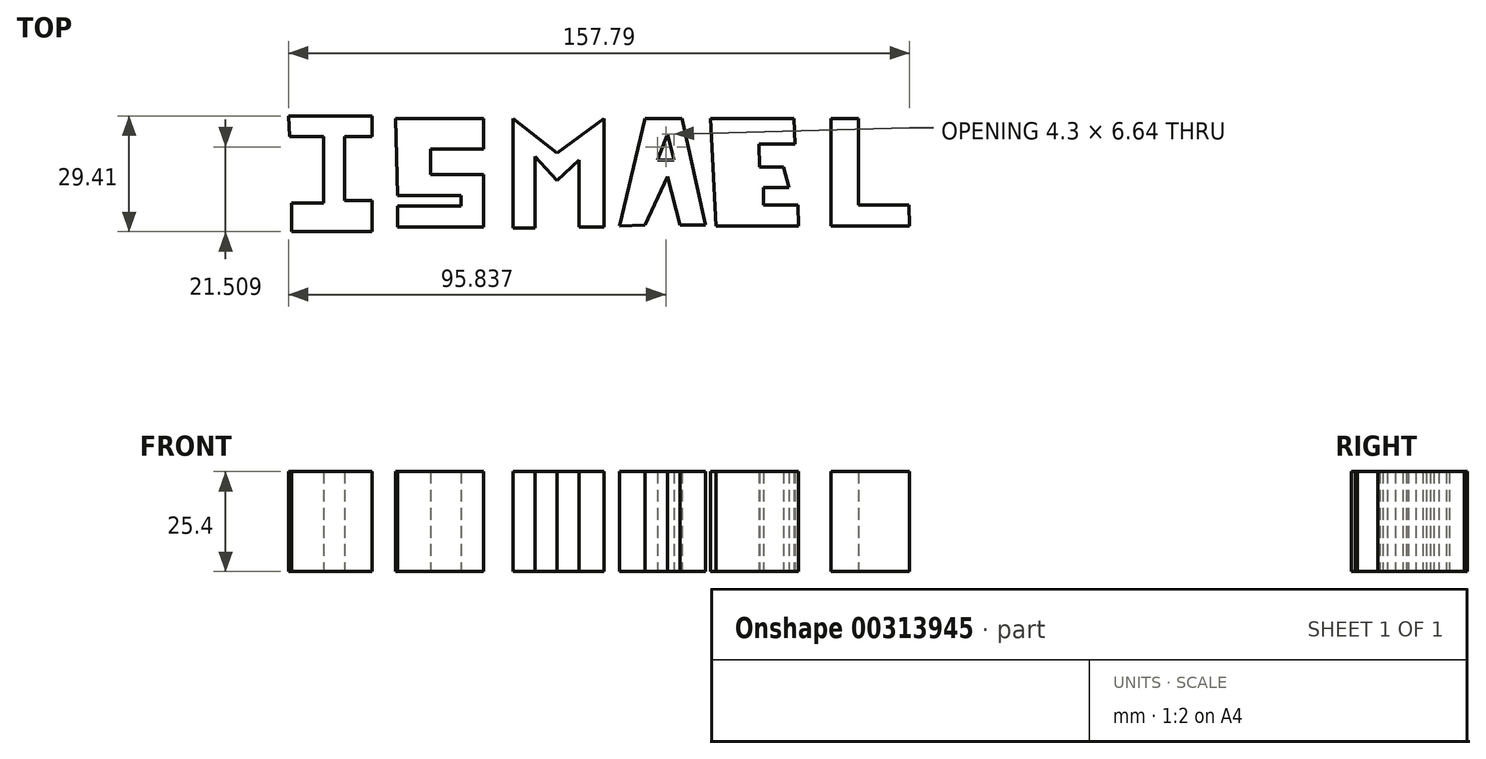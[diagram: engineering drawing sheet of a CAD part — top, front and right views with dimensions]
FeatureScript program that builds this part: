
annotation { "Feature Type Name" : "Feature", "Feature Type Description" : "" }
export const myFeature = defineFeature(function(context is Context, id is Id, definition is map)
    precondition{}
    {
        {
            var Q0;
            Q0=qCreatedBy(makeId("Top.planeOp"),FACE);
            var sketch = newSketch(context, id + "F0", { "sketchPlane" : qUnion([Q0])});
            skLineSegment(sketch, "E0", {"start": v(-96.24, 33.02) * mm, "end": v(-75.04, 33.02) * mm});
            skLineSegment(sketch, "E1", {"start": v(-75.04, 33.02) * mm, "end": v(-75.04, 27.71) * mm});
            skLineSegment(sketch, "E2", {"start": v(-75.04, 27.71) * mm, "end": v(-82.03, 27.71) * mm});
            skLineSegment(sketch, "E3", {"start": v(-82.03, 27.71) * mm, "end": v(-82.03, 11.57) * mm});
            skLineSegment(sketch, "E4", {"start": v(-82.03, 11.57) * mm, "end": v(-75.04, 11.57) * mm});
            skLineSegment(sketch, "E5", {"start": v(-75.04, 11.57) * mm, "end": v(-75.04, 3.61) * mm});
            skLineSegment(sketch, "E6", {"start": v(-75.04, 3.61) * mm, "end": v(-95.52, 3.61) * mm});
            skLineSegment(sketch, "E7", {"start": v(-95.52, 3.61) * mm, "end": v(-95.52, 10.84) * mm});
            skLineSegment(sketch, "E8", {"start": v(-95.52, 10.84) * mm, "end": v(-87.33, 10.84) * mm});
            skLineSegment(sketch, "E9", {"start": v(-87.33, 10.84) * mm, "end": v(-87.33, 27.71) * mm});
            skLineSegment(sketch, "E10", {"start": v(-87.33, 27.71) * mm, "end": v(-96, 27.71) * mm});
            skLineSegment(sketch, "E11", {"start": v(-96, 27.71) * mm, "end": v(-96.24, 33.02) * mm});
            skSolve(sketch);
        }
        {
            var Q0;
            Q0=makeQuery(id+"F0.imprint","IMPRINT",FACE,{"disambiguationData":[TD([[makeQuery(id+"F0.imprint","IMPRINT",EDGE,{"derivedFrom":sQuery(id+"F0.wireOp",EDGE,"E0")}),-1.0]])]});
            extrude(context, id + "F1", {"entities" : qUnion([Q0]), "depth" : 25.4 * mm});
        }
        {
            var Q0;
            Q0=qCreatedBy(makeId("Top.planeOp"),FACE);
            var sketch = newSketch(context, id + "F2", { "sketchPlane" : qUnion([Q0])});
            skLineSegment(sketch, "E12", {"start": v(-69.07, 32.3) * mm, "end": v(-46.65, 32.3) * mm});
            skLineSegment(sketch, "E13", {"start": v(-46.65, 32.3) * mm, "end": v(-46.65, 24.58) * mm});
            skLineSegment(sketch, "E14", {"start": v(-46.65, 24.58) * mm, "end": v(-60.15, 24.58) * mm});
            skLineSegment(sketch, "E15", {"start": v(-60.15, 24.58) * mm, "end": v(-60.15, 18.07) * mm});
            skLineSegment(sketch, "E16", {"start": v(-60.15, 18.07) * mm, "end": v(-46.65, 18.07) * mm});
            skLineSegment(sketch, "E17", {"start": v(-46.65, 18.07) * mm, "end": v(-46.65, 4.82) * mm});
            skLineSegment(sketch, "E18", {"start": v(-46.65, 4.82) * mm, "end": v(-68.58, 4.82) * mm});
            skLineSegment(sketch, "E19", {"start": v(-68.58, 4.82) * mm, "end": v(-68.58, 10.12) * mm});
            skLineSegment(sketch, "E20", {"start": v(-68.58, 10.12) * mm, "end": v(-52.44, 10.12) * mm});
            skLineSegment(sketch, "E21", {"start": v(-52.44, 10.12) * mm, "end": v(-52.44, 12.77) * mm});
            skLineSegment(sketch, "E22", {"start": v(-52.44, 12.77) * mm, "end": v(-68.58, 12.77) * mm});
            skLineSegment(sketch, "E23", {"start": v(-68.58, 12.77) * mm, "end": v(-69.07, 32.3) * mm});
            skLineSegment(sketch, "E24", {"start": v(-39.18, 32.3) * mm, "end": v(-39.18, 4.58) * mm});
            skLineSegment(sketch, "E25", {"start": v(-39.18, 4.58) * mm, "end": v(-33.64, 4.58) * mm});
            skLineSegment(sketch, "E26", {"start": v(-33.64, 4.58) * mm, "end": v(-33.64, 22.65) * mm});
            skLineSegment(sketch, "E27", {"start": v(-33.64, 22.65) * mm, "end": v(-28.1, 16.63) * mm});
            skLineSegment(sketch, "E28", {"start": v(-28.1, 16.63) * mm, "end": v(-22.47, 21.8) * mm});
            skLineSegment(sketch, "E29", {"start": v(-22.47, 21.8) * mm, "end": v(-22.47, 4.82) * mm});
            skLineSegment(sketch, "E30", {"start": v(-22.47, 4.82) * mm, "end": v(-16.05, 4.82) * mm});
            skLineSegment(sketch, "E31", {"start": v(-16.05, 4.82) * mm, "end": v(-16.05, 32.3) * mm});
            skLineSegment(sketch, "E32", {"start": v(-16.05, 32.3) * mm, "end": v(-28.1, 23.62) * mm});
            skLineSegment(sketch, "E33", {"start": v(-28.1, 23.62) * mm, "end": v(-39.18, 32.3) * mm});
            skLineSegment(sketch, "E34", {"start": v(-12.2, 5.06) * mm, "end": v(-5.68, 32.3) * mm});
            skLineSegment(sketch, "E35", {"start": v(-5.68, 32.3) * mm, "end": v(3.71, 32.3) * mm});
            skLineSegment(sketch, "E36", {"start": v(3.71, 32.3) * mm, "end": v(9.74, 5.3) * mm});
            skLineSegment(sketch, "E37", {"start": v(9.74, 5.3) * mm, "end": v(3.23, 5.3) * mm});
            skLineSegment(sketch, "E38", {"start": v(3.23, 5.3) * mm, "end": v(0, 17.6) * mm});
            skLineSegment(sketch, "E39", {"start": v(0, 17.6) * mm, "end": v(-5.68, 5.3) * mm});
            skLineSegment(sketch, "E40", {"start": v(-5.68, 5.3) * mm, "end": v(-12.2, 5.06) * mm});
            skLineSegment(sketch, "E41", {"start": v(-2.55, 21.8) * mm, "end": v(0, 28.44) * mm});
            skLineSegment(sketch, "E42", {"start": v(0, 28.44) * mm, "end": v(1.75, 21.8) * mm});
            skLineSegment(sketch, "E43", {"start": v(1.75, 21.8) * mm, "end": v(-2.55, 21.8) * mm});
            skLineSegment(sketch, "E44", {"start": v(10.94, 32.3) * mm, "end": v(32.15, 32.3) * mm});
            skLineSegment(sketch, "E45", {"start": v(32.15, 32.3) * mm, "end": v(32.4, 25.81) * mm});
            skLineSegment(sketch, "E46", {"start": v(32.4, 25.81) * mm, "end": v(23.23, 25.81) * mm});
            skLineSegment(sketch, "E47", {"start": v(23.23, 25.81) * mm, "end": v(23.45, 20.04) * mm});
            skLineSegment(sketch, "E48", {"start": v(23.45, 20.04) * mm, "end": v(29.5, 20.04) * mm});
            skLineSegment(sketch, "E49", {"start": v(29.5, 20.04) * mm, "end": v(30.89, 14.76) * mm});
            skLineSegment(sketch, "E50", {"start": v(30.89, 14.76) * mm, "end": v(24.44, 14.76) * mm});
            skLineSegment(sketch, "E51", {"start": v(24.44, 14.76) * mm, "end": v(24.44, 10.36) * mm});
            skLineSegment(sketch, "E52", {"start": v(24.44, 10.36) * mm, "end": v(33.12, 10.36) * mm});
            skLineSegment(sketch, "E53", {"start": v(33.12, 10.36) * mm, "end": v(33.31, 5.06) * mm});
            skLineSegment(sketch, "E54", {"start": v(33.31, 5.06) * mm, "end": v(12.4, 5.06) * mm});
            skLineSegment(sketch, "E55", {"start": v(12.4, 5.06) * mm, "end": v(10.94, 32.3) * mm});
            skLineSegment(sketch, "E56", {"start": v(41.55, 32.3) * mm, "end": v(41.55, 5.06) * mm});
            skPoint(sketch, "E56.startSnap0", {"position": v(21.55, 32.3) * mm});
            skLineSegment(sketch, "E57", {"start": v(41.55, 5.06) * mm, "end": v(61.55, 5.06) * mm});
            skLineSegment(sketch, "E58", {"start": v(61.55, 5.06) * mm, "end": v(61.36, 10.36) * mm});
            skLineSegment(sketch, "E59", {"start": v(61.36, 10.36) * mm, "end": v(48.54, 10.36) * mm});
            skLineSegment(sketch, "E60", {"start": v(48.54, 10.36) * mm, "end": v(48.54, 32.3) * mm});
            skLineSegment(sketch, "E61", {"start": v(48.54, 32.3) * mm, "end": v(41.55, 32.3) * mm});
            skSolve(sketch);
        }
        {
            var Q0;
            Q0 = qSketchRegion(id + "F2", true);
            extrude(context, id + "F3", {"entities" : qUnion([Q0]), "depth" : 25.4 * mm});
        }
    });
